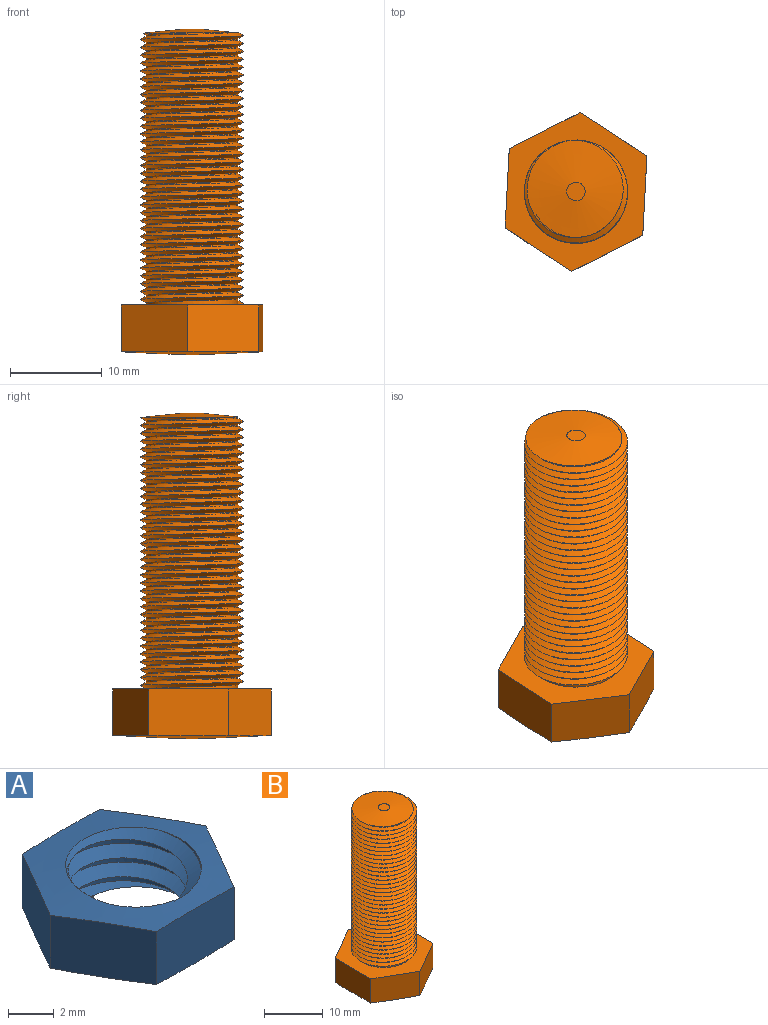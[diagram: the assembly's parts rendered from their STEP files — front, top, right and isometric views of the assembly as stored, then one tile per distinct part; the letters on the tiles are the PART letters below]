
ASSEMBLY  parts=2 mates=1
PART A: 13 faces, bbox 9.6x9.6x4 mm
  f0: cylinder r=3.2mm len=6.4mm, axis (0,0,1), area 18.4mm2, adj f1,f2,f9,f10
  f1: cone r=6.6mm half-angle=85.6deg, axis (0,0,1), area 31.4mm2, adj f0,f3,f4,f5,f6,f7,f8,f9
  f2: cone r=6.6mm half-angle=85.6deg, axis (0,0,-1), area 31.5mm2, adj f0,f3,f4,f5,f6,f7,f8,f9
  f3: plane 4.15x2.91mm, normal (0.87,-0.5,0), area 13.8mm2, adj f1,f2,f4,f8
  f4: plane 4.15x2.91mm, normal (0.87,0.5,0), area 13.8mm2, adj f1,f2,f3,f5
  f5: plane 4.79x2.92mm, normal (0,1,0), area 13.8mm2, adj f1,f2,f4,f6
  f6: plane 4.15x2.91mm, normal (-0.87,0.5,0), area 13.8mm2, adj f1,f2,f5,f7
  f7: plane 4.15x2.91mm, normal (-0.87,-0.5,0), area 13.8mm2, adj f1,f2,f6,f8
  f8: plane 4.79x2.92mm, normal (0,-1,0), area 13.8mm2, adj f1,f2,f3,f7
  f9: bspline ~7.39x6.4mm, area 39.2mm2, adj f0,f1,f2,f10,f11,f12
  f10: bspline ~7.39x6.4mm, area 39.3mm2, adj f0,f1,f2,f9,f11,f12
  f11: bspline ~4.39x3.19mm, area 0.2mm2, adj f1,f9,f10
  f12: cone r=2.85mm half-angle=45deg, axis (0,0,1), area 0.1mm2, adj f2,f9,f10
PART B: 14 faces, bbox 17.9x17.9x36.1 mm
  f0: cylinder r=5mm len=29.6mm, axis (0,0,-1), area 232.9mm2, adj f1,f2,f9,f11,f12
  f1: bspline ~30.21x12.95mm, area 802.9mm2, adj f0,f2,f9,f11,f12
  f2: bspline ~29.78x12.95mm, area 795.7mm2, adj f0,f1,f11,f12
  f3: plane 7.5x5.11mm, normal (-0.5,0.87,0), area 44mm2, adj f4,f8,f9,f10
  f4: plane 7.5x5.11mm, normal (0.5,0.87,0), area 44mm2, adj f3,f5,f9,f10
  f5: plane 9.28x5.73mm, normal (1,0,0), area 44mm2, adj f4,f6,f9,f10
  f6: plane 7.5x5.11mm, normal (0.5,-0.87,0), area 44mm2, adj f5,f7,f9,f10
  f7: plane 7.5x5.11mm, normal (-0.5,-0.87,0), area 44mm2, adj f6,f8,f9,f10
  f8: plane 8.66x5.11mm, normal (-1,0,0), area 44mm2, adj f3,f7,f9,f10
  f9: plane 17.5x15.18mm, normal (0,0,1), area 115.2mm2, adj f0,f1,f3,f4,f5,f6,f7,f8
  f10: revolved ~17.32x17.32mm, area 196.8mm2, adj f3,f4,f5,f6,f7,f8
  f11: plane 0.61x0.51mm, normal (0,-1,0), area 0.2mm2, adj f0,f1,f2,f9
  f12: cone r=6.02mm half-angle=84.3deg, axis (0,0,-1), area 83.9mm2, adj f0,f1,f2,f13
  f13: plane 2x2mm, normal (0,0,1), area 3.1mm2, adj f12
PLACE A t=(-4.93,1.85,18.41)mm
PLACE B rot(axis=(0,0,-1),3deg) t=(-4.93,1.85,4.39)mm
MATE cylindrical A.f0 <-> B.f0  axis (0,0,1) through (-4.93,1.85,20.19)mm
